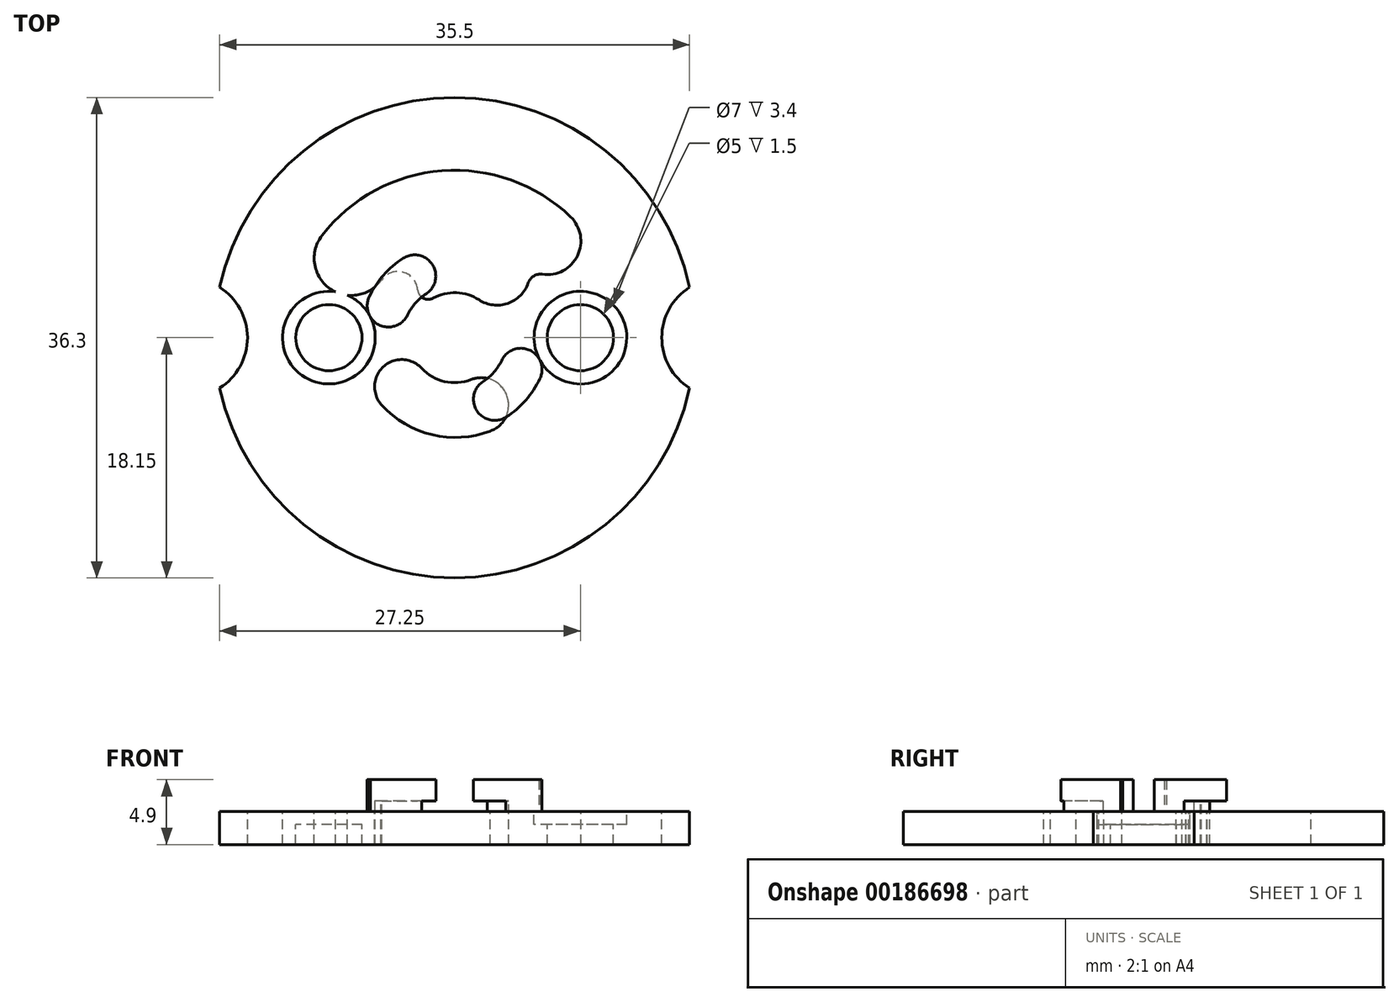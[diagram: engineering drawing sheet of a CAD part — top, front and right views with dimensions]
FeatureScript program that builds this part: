
annotation { "Feature Type Name" : "Feature", "Feature Type Description" : "" }
export const myFeature = defineFeature(function(context is Context, id is Id, definition is map)
    precondition{}
    {
        {
            var Q0;
            Q0=qCreatedBy(makeId("Top.planeOp"),FACE);
            var sketch = newSketch(context, id + "F0", { "sketchPlane" : qUnion([Q0])});
            skArc(sketch, "E0", {"start": v(-17.75, -3.8) * mm, "mid": v(0, -18.15) * mm, "end": v(17.75, -3.8) * mm});
            skArc(sketch, "E1", {"start": v(10.03, 7.71) * mm, "mid": v(0.95, 12.61) * mm, "end": v(-8.76, 9.13) * mm});
            skArc(sketch, "E2", {"start": v(1.62, 2.99) * mm, "mid": v(-0.13, 3.4) * mm, "end": v(-1.85, 2.85) * mm});
            skArc(sketch, "E3", {"start": v(-8.76, 9.13) * mm, "mid": v(-9.28, 6.19) * mm, "end": v(-6.64, 4.79) * mm});
            skArc(sketch, "E4", {"start": v(5.57, 4.29) * mm, "mid": v(9.51, 3.77) * mm, "end": v(10.03, 7.71) * mm});
            skArc(sketch, "E5", {"start": v(5.5, -5.1) * mm, "mid": v(5.4, -2.2) * mm, "end": v(2.5, -2.3) * mm});
            skArc(sketch, "E6", {"start": v(-1.24, -3.17) * mm, "mid": v(-3.95, -4.37) * mm, "end": v(-2.7, -7.06) * mm});
            skArc(sketch, "E7", {"start": v(-5.55, 4.13) * mm, "mid": v(-4, 2.59) * mm, "end": v(-1.85, 2.85) * mm});
            skArc(sketch, "E8", {"start": v(1.62, 2.99) * mm, "mid": v(2.38, 2.99) * mm, "end": v(2.8, 3.62) * mm});
            skArc(sketch, "E9.trimOffspring", {"start": v(-2.7, -7.06) * mm, "mid": v(1.7, -7.34) * mm, "end": v(5.5, -5.1) * mm});
            skArc(sketch, "E10.trimOffspring", {"start": v(-1.24, -3.17) * mm, "mid": v(0.76, -3.31) * mm, "end": v(2.5, -2.3) * mm});
            skArc(sketch, "E11", {"start": v(-5.55, 4.13) * mm, "mid": v(-5.98, 4.65) * mm, "end": v(-6.64, 4.79) * mm});
            skArc(sketch, "E12", {"start": v(5.51, 4.37) * mm, "mid": v(3.9, 4.95) * mm, "end": v(2.8, 3.62) * mm});
            skArc(sketch, "E13", {"start": v(-17.75, -3.8) * mm, "mid": v(-15.65, 0) * mm, "end": v(-17.75, 3.8) * mm});
            skArc(sketch, "E14.MirrorCS", {"start": v(17.75, -3.8) * mm, "mid": v(15.65, 0) * mm, "end": v(17.75, 3.8) * mm});
            skArc(sketch, "E15.trimOffspring", {"start": v(17.75, 3.8) * mm, "mid": v(0, 18.15) * mm, "end": v(-17.75, 3.8) * mm});
            skLineSegment(sketch, "E16", {"start": v(5.51, 4.37) * mm, "end": v(5.57, 4.29) * mm});
            skSolve(sketch);
        }
        {
            var Q0;
            Q0=makeQuery(id+"F0.imprint","IMPRINT",FACE,{"disambiguationData":[TD([[makeQuery(id+"F0.imprint","IMPRINT",EDGE,{"derivedFrom":sQuery(id+"F0.wireOp",EDGE,"E0")}),1.0]])]});
            extrude(context, id + "F1", {"entities" : qUnion([Q0]), "depth" : 2.5 * mm});
        }
        {
            var Q0;
            Q0=makeQuery(id+"F1.opExtrude","CAP_FACE",FACE,{"disambiguationData":[OSD([sQuery(id+"F0.wireOp",EDGE,"E0"),sQuery(id+"F0.wireOp",EDGE,"E5"),sQuery(id+"F0.wireOp",EDGE,"E6"),sQuery(id+"F0.wireOp",EDGE,"E9.trimOffspring"),sQuery(id+"F0.wireOp",EDGE,"E10.trimOffspring"),sQuery(id+"F0.wireOp",EDGE,"E13"),sQuery(id+"F0.wireOp",EDGE,"E14.MirrorCS"),sQuery(id+"F0.wireOp",EDGE,"E15.trimOffspring")])],"isStart":true});
            var sketch = newSketch(context, id + "F2", { "sketchPlane" : qUnion([Q0])});
            skCircle(sketch, "E17", {"center": v(-9.5, 0) * mm, "radius": 2.5 * mm});
            skCircle(sketch, "E18.MirrorC", {"center": v(9.5, 0) * mm, "radius": 2.5 * mm});
            skCircle(sketch, "E19", {"center": v(9.5, 0) * mm, "radius": 3.5 * mm});
            skCircle(sketch, "E20.MirrorC", {"center": v(-9.5, 0) * mm, "radius": 3.5 * mm});
            skSolve(sketch);
        }
        {
            var Q0;
            Q0=makeQuery(id+"F2.imprint","IMPRINT",FACE,{"disambiguationData":[TD([[makeQuery(id+"F2.imprint","IMPRINT",EDGE,{"derivedFrom":sQuery(id+"F2.wireOp",EDGE,"E18.MirrorC")}),1.0]])]});
            var Q1;
            Q1=makeQuery(id+"F2.imprint","IMPRINT",FACE,{"disambiguationData":[TD([[makeQuery(id+"F2.imprint","IMPRINT",EDGE,{"derivedFrom":sQuery(id+"F2.wireOp",EDGE,"E17")}),-1.0]])]});
            var Q2;
            Q2=sQuery(id+"F2.wireOp",EDGE,"E20.MirrorC");
            var Q3;
            Q3=sQuery(id+"F2.wireOp",EDGE,"E19");
            extrude(context, id + "F3", {"entities" : qUnion([Q0, Q1]), "operationType" : NewBodyOperationType.REMOVE, "surfaceEntities" : qUnion([Q2, Q3]), "oppositeDirection" : true, "depth" : 1 * mm});
        }
        {
            var Q0;
            Q0=makeQuery(id+"F2.imprint","IMPRINT",FACE,{"disambiguationData":[TD([[makeQuery(id+"F2.imprint","IMPRINT",EDGE,{"derivedFrom":sQuery(id+"F2.wireOp",EDGE,"E18.MirrorC")}),-1.0]])]});
            var Q1;
            Q1=makeQuery(id+"F2.imprint","IMPRINT",FACE,{"disambiguationData":[TD([[makeQuery(id+"F2.imprint","IMPRINT",EDGE,{"derivedFrom":sQuery(id+"F2.wireOp",EDGE,"E17")}),1.0]])]});
            extrude(context, id + "F4", {"entities" : qUnion([Q0, Q1]), "operationType" : NewBodyOperationType.REMOVE, "oppositeDirection" : true, "depth" : 25 * mm});
        }
        {
            var Q0;
            Q0=makeQuery(id+"F1.opExtrude","CAP_FACE",FACE,{"disambiguationData":[OSD([sQuery(id+"F0.wireOp",EDGE,"E0"),sQuery(id+"F0.wireOp",EDGE,"E1"),sQuery(id+"F0.wireOp",EDGE,"E2"),sQuery(id+"F0.wireOp",EDGE,"E3"),sQuery(id+"F0.wireOp",EDGE,"E4"),sQuery(id+"F0.wireOp",EDGE,"E5"),sQuery(id+"F0.wireOp",EDGE,"E6"),sQuery(id+"F0.wireOp",EDGE,"E7"),sQuery(id+"F0.wireOp",EDGE,"E8"),sQuery(id+"F0.wireOp",EDGE,"E9.trimOffspring"),sQuery(id+"F0.wireOp",EDGE,"E10.trimOffspring"),sQuery(id+"F0.wireOp",EDGE,"E11"),sQuery(id+"F0.wireOp",EDGE,"E12")])],"isStart":true});
            var sketch = newSketch(context, id + "F5", { "sketchPlane" : qUnion([Q0])});
            skArc(sketch, "E21", {"start": v(-3.9, 6) * mm, "mid": v(-5.37, 4.72) * mm, "end": v(-6.45, 3.1) * mm});
            skArc(sketch, "E22", {"start": v(-2.15, 3.31) * mm, "mid": v(-2.97, 2.6) * mm, "end": v(-3.56, 1.7) * mm});
            skArc(sketch, "E23", {"start": v(6.45, -3.1) * mm, "mid": v(5.7, -0.96) * mm, "end": v(3.56, -1.7) * mm});
            skArc(sketch, "E24", {"start": v(-2.15, 3.31) * mm, "mid": v(-1.68, 5.53) * mm, "end": v(-3.9, 6) * mm});
            skArc(sketch, "E25", {"start": v(-6.45, 3.1) * mm, "mid": v(-5.7, 0.96) * mm, "end": v(-3.56, 1.7) * mm});
            skArc(sketch, "E26", {"start": v(2.15, -3.31) * mm, "mid": v(1.68, -5.53) * mm, "end": v(3.9, -6) * mm});
            skArc(sketch, "E27.trimOffspring", {"start": v(2.15, -3.31) * mm, "mid": v(2.97, -2.6) * mm, "end": v(3.56, -1.7) * mm});
            skArc(sketch, "E28.trimOffspring", {"start": v(3.9, -6) * mm, "mid": v(5.37, -4.72) * mm, "end": v(6.45, -3.1) * mm});
            skPoint(sketch, "E29.endSnap0", {"position": v(0, 18.15) * mm});
            skLineSegment(sketch, "E30", {"start": v(0, -20.52) * mm, "end": v(0, 20.52) * mm, "construction": true});
            skSolve(sketch);
        }
        {
            var Q0;
            {var subQ1=sQuery(id+"F5.wireOp",EDGE,"E23");Q0=makeQuery(id+"F5.imprint","IMPRINT",FACE,{"disambiguationData":[TD([[makeQuery(id+"F5.imprint","IMPRINT",EDGE,{"derivedFrom":subQ1}),1.0]])]});}
            var Q1;
            {var subQ0=makeQuery(id+"F1.opExtrude","CAP_EDGE",EDGE,{"disambiguationData":[OSD([sQuery(id+"F0.wireOp",EDGE,"E12")])],"isStart":true});Q1=makeQuery(id+"F5.imprint","IMPRINT",FACE,{"disambiguationData":[TD([[makeQuery(id+"F5.imprint","IMPRINT",EDGE,{"derivedFrom":subQ0}),1.0]])]});}
            var Q2;
            {var subQ1=sQuery(id+"F5.wireOp",EDGE,"E21");Q2=makeQuery(id+"F5.imprint","IMPRINT",FACE,{"disambiguationData":[TD([[makeQuery(id+"F5.imprint","IMPRINT",EDGE,{"derivedFrom":subQ1}),1.0]])]});}
            var Q3;
            {var subQ0=sQuery(id+"F5.wireOp",EDGE,"E24");var subQ1=makeQuery(id+"F1.opExtrude","CAP_EDGE",EDGE,{"disambiguationData":[OSD([sQuery(id+"F0.wireOp",EDGE,"E6")])],"isStart":true});var subQ2=makeQuery(id+"F5.imprint","INTERSECT",VERTEX,{"disambiguationData":[OD(0.0)],"derivedFrom":[subQ1,subQ0]});Q3=makeQuery(id+"F5.imprint","IMPRINT",FACE,{"disambiguationData":[TD([[makeQuery(id+"F5.imprint","IMPRINT",EDGE,{"disambiguationData":[TD([[subQ2,-1.0]])],"derivedFrom":subQ0}),1.0]])]});}
            var Q4;
            {var subQ5=sQuery(id+"F5.wireOp",EDGE,"E22");Q4=makeQuery(id+"F5.imprint","IMPRINT",FACE,{"disambiguationData":[TD([[makeQuery(id+"F5.imprint","IMPRINT",EDGE,{"derivedFrom":subQ5}),-1.0]])]});}
            var Q5;
            {var subQ6=sQuery(id+"F5.wireOp",EDGE,"E27.trimOffspring");Q5=makeQuery(id+"F5.imprint","IMPRINT",FACE,{"disambiguationData":[TD([[makeQuery(id+"F5.imprint","IMPRINT",EDGE,{"derivedFrom":subQ6}),-1.0]])]});}
            extrude(context, id + "F6", {"entities" : qUnion([Q0, Q1, Q2, Q3, Q4, Q5]), "operationType" : NewBodyOperationType.ADD, "depth" : 2.4 * mm});
        }
        {
            var Q0;
            Q0=makeQuery(id+"F6.opExtrude","CAP_FACE",FACE,{"disambiguationData":[OSD([sQuery(id+"F2.wireOp",EDGE,"E19"),sQuery(id+"F5.wireOp",EDGE,"E23"),sQuery(id+"F5.wireOp",EDGE,"E26"),sQuery(id+"F5.wireOp",EDGE,"E27.trimOffspring"),sQuery(id+"F5.wireOp",EDGE,"E28.trimOffspring")])],"isStart":true});
            var Q1;
            Q1=makeQuery(id+"F6.opExtrude","CAP_FACE",FACE,{"disambiguationData":[OSD([sQuery(id+"F2.wireOp",EDGE,"E20.MirrorC"),sQuery(id+"F5.wireOp",EDGE,"E21"),sQuery(id+"F5.wireOp",EDGE,"E22"),sQuery(id+"F5.wireOp",EDGE,"E24"),sQuery(id+"F5.wireOp",EDGE,"E25")])],"isStart":true});
            extrude(context, id + "F7", {"entities" : qUnion([Q0, Q1]), "operationType" : NewBodyOperationType.REMOVE, "oppositeDirection" : true, "depth" : 0.8 * mm});
        }
        {
            var Q0;
            Q0=makeQuery(id+"F1.opExtrude","SWEPT_BODY",BODY,{"disambiguationData":[OSD([sQuery(id+"F0.wireOp",EDGE,"E0"),sQuery(id+"F0.wireOp",EDGE,"E1"),sQuery(id+"F0.wireOp",EDGE,"E2"),sQuery(id+"F0.wireOp",EDGE,"E3"),sQuery(id+"F0.wireOp",EDGE,"E4"),sQuery(id+"F0.wireOp",EDGE,"E5"),sQuery(id+"F0.wireOp",EDGE,"E6"),sQuery(id+"F0.wireOp",EDGE,"E7"),sQuery(id+"F0.wireOp",EDGE,"E8"),sQuery(id+"F0.wireOp",EDGE,"E9.trimOffspring"),sQuery(id+"F0.wireOp",EDGE,"E10.trimOffspring"),sQuery(id+"F0.wireOp",EDGE,"E11"),sQuery(id+"F0.wireOp",EDGE,"E12"),sQuery(id+"F0.wireOp",EDGE,"E13"),sQuery(id+"F0.wireOp",EDGE,"E14.MirrorCS"),sQuery(id+"F0.wireOp",EDGE,"E15.trimOffspring"),sQuery(id+"F0.wireOp",EDGE,"E16")])]});
            var Q1;
            Q1=sQuery(id+"F5.wireOp",EDGE,"E30");
            var Q2;
            Q2=sQuery(id+"F5.wireOp",EDGE,"E30");
            transform(context, id + "F8", {"entities" : qUnion([Q0]), "transformType" : TransformType.ROTATION, "transformAxis" : qUnion([Q2]), "angle" : 180 * degree, "makeCopy" : false});
        }
    });
